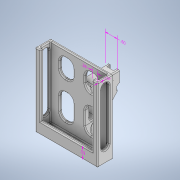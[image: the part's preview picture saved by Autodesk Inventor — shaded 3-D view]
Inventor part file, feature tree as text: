
AUTODESK INVENTOR PART (.ipt)
format: ipt  version: 2020 (Build 240168000, 168)  size: 820,224 bytes
history: native  units: in
note: dims shown in document units (in); Inventor stores cm internally (conversion verified against a paired STEP export)
features: sketch x11, extrude x9, chamfer x7, other x5, fillet x5, hole x2
ambient origin geometry x8: Origin, YZ Plane, XZ Plane, XY Plane, X Axis, Y Axis, Z Axis, Center Point
bodies: Solid1 (feature_tree)
feature tree (39):
  other  "Annotations"
  extrude  "Extrusion1"  Depth=0.8in
  extrude  "Extrusion2"  Depth=0.15in
  extrude  "Extrusion3"  Depth=0.15in
  extrude  "Extrusion4"  Depth=3.6in TaperAngle=0.0deg
  extrude  "Extrusion5"  Depth=0.42in
  extrude  "Extrusion6"  Depth=0.28in
  chamfer  "Chamfer1"  Distance=0.15in
  extrude  "Extrusion7"  Depth=0.59in
  sketch  "Sketch9"  dims[d26=0.2in d27=0.2in]
  sketch  "Sketch10"  dims[d28=4.0in d29=0.0in d30=0.3in]
  extrude  "Extrusion8"  Depth=0.2in
  extrude  "Extrusion9"  Depth=0.3in
  chamfer  "Chamfer2"  Distance=0.7in
  chamfer  "Chamfer3"  Distance=0.7in
  chamfer  "Chamfer4"  Distance=0.35in
  chamfer  "Chamfer5"  Distance=1.0in
  chamfer  "Chamfer6"  Distance=1.5in
  chamfer  "Chamfer7"  Distance=1.8in Angle=45.0deg
  fillet  "Fillet1"  Radius=0.3in
  fillet  "Fillet2"  Radius=0.3in
  fillet  "Fillet3"  Radius=1.0in
  fillet  "Fillet4"  Radius=0.125in
  hole  "Hole1"  [1 undecoded]
  hole  "Hole2"  [1 undecoded]
  fillet  "Fillet6"  Radius=0.125in
  sketch  "Sketch1"  dims[d0=3.2in d1=0.8in]
  sketch  "Sketch2"  dims[d2=0.17in d3=0.0in d4=0.15in]
  sketch  "Sketch4"  dims[d5=0.15in d6=0.15in]
  sketch  "Sketch5"  dims[d7=0.15in d8=3.6in d9=0.0in]
  sketch  "Sketch6"  dims[d10=0.17in d11=0.42in]
  sketch  "Sketch7"  dims[d12=0.28in d13=0.28in d14=0.15in d15=0.0in]
  sketch  "Sketch8"  dims[d24=0.2in d25=0.59in]
  sketch  "Sketch11"  dims[d31=0.6in]
  sketch  "Sketch12"  dims[d32=0.6in d34=0.7in d35=0.7in d36=0.35in d37=1.0in d38=0.0in d39=1.5in d40=0.0in d41=1.8in d42=1.5in d43=45.0deg d44=0.3in d45=0.3in d46=1.0in d47=0.0in d51=0.125in d52=0.125in d53=0.125in d54=0.125in d55=0.13in d56=0.0in d57=0.13in d58=0.0in d59=0.2in d60=0.13in d61=45.0deg d62=0.2in d63=0.13in d64=45.0deg d65=0.1in d66=0.13in d67=45.0deg d68=0.1in d69=0.13in d70=45.0deg d71=0.1in d72=0.13in d73=45.0deg d74=0.1in d75=0.13in d76=45.0deg d77=0.2in d78=0.3in d79=0.05in d80=0.05in d82=0.061in d83=0.061in d84=0.12in d85=0.75in d86=0.119in d87=0.25in d88=0.5635in d89=0.3in d90=0.8108in d91=0.061in d92=0.3in d93=0.061in d94=0.061in d95=0.3in d96=0.061in d97=0.3in d98=0.12in d99=0.75in d100=0.119in d101=0.25in d102=0.5635in d103=0.3in d104=0.8108in d105=0.04in d16=0.1873in d17=0.2224in d18=0.59in d19=0.3645in d20=0.0277in d21=0.28in d22=0.1162in d23=0.15in d48=0.1879in d49=0.1703in d50=0.6in]
  other  "Linear Dimension 1"
  other  "Linear Dimension 2"
  other  "Linear Dimension 3"
  other  "Linear Dimension 4"
note: 2 required parameter values undecoded (feature->parameter linkage not recoverable at this tier; creation-order binding heuristic only, values carry confidence <= 0.55)
